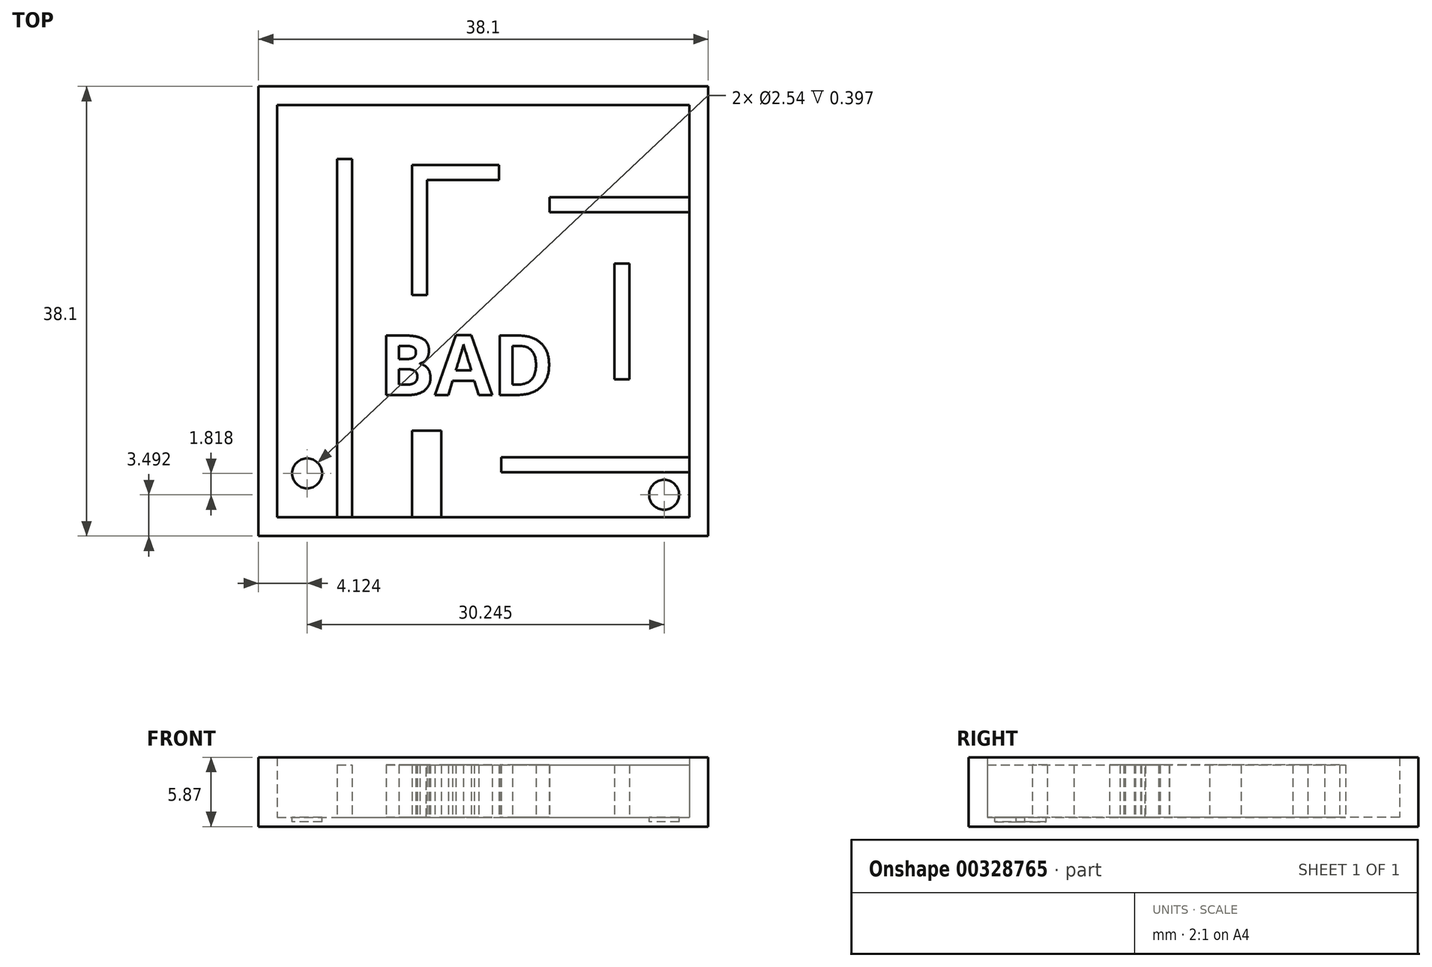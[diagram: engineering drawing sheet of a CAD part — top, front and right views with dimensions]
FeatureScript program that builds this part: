
annotation { "Feature Type Name" : "Feature", "Feature Type Description" : "" }
export const myFeature = defineFeature(function(context is Context, id is Id, definition is map)
    precondition{}
    {
        {
            var Q0;
            Q0=qCreatedBy(makeId("Top.planeOp"),FACE);
            var sketch = newSketch(context, id + "F0", { "sketchPlane" : qUnion([Q0])});
            skLineSegment(sketch, "E0.bottom", {"start": v(-16.01, 14.3) * mm, "end": v(22.09, 14.3) * mm});
            skLineSegment(sketch, "E0.top", {"start": v(-16.01, -23.8) * mm, "end": v(22.09, -23.8) * mm});
            skLineSegment(sketch, "E0.left", {"start": v(-16.01, 14.3) * mm, "end": v(-16.01, -23.8) * mm});
            skLineSegment(sketch, "E0.right", {"start": v(22.09, 14.3) * mm, "end": v(22.09, -23.8) * mm});
            skSolve(sketch);
        }
        {
            var Q0;
            Q0=makeQuery(id+"F0.imprint","IMPRINT",FACE,{"disambiguationData":[TD([[makeQuery(id+"F0.imprint","IMPRINT",EDGE,{"derivedFrom":sQuery(id+"F0.wireOp",EDGE,"E0.bottom")}),-1.0]])]});
            extrude(context, id + "F1", {"entities" : qUnion([Q0]), "depth" : 0.8 * mm});
        }
        {
            var Q0;
            Q0=makeQuery(id+"F1.opExtrude","CAP_FACE",FACE,{"disambiguationData":[OSD([sQuery(id+"F0.wireOp",EDGE,"E0.bottom"),sQuery(id+"F0.wireOp",EDGE,"E0.top"),sQuery(id+"F0.wireOp",EDGE,"E0.left"),sQuery(id+"F0.wireOp",EDGE,"E0.right")])],"isStart":false});
            var sketch = newSketch(context, id + "F2", { "sketchPlane" : qUnion([Q0])});
            skLineSegment(sketch, "E1.0", {"start": v(-14.43, 12.71) * mm, "end": v(20.5, 12.71) * mm});
            skLineSegment(sketch, "E1.1", {"start": v(-14.43, 12.71) * mm, "end": v(-14.43, -22.21) * mm});
            skLineSegment(sketch, "E1.2", {"start": v(-14.43, -22.21) * mm, "end": v(20.5, -22.21) * mm});
            skLineSegment(sketch, "E1.3", {"start": v(20.5, 12.71) * mm, "end": v(20.5, -22.21) * mm});
            skSolve(sketch);
        }
        {
            var Q0;
            Q0=makeQuery(id+"F2.imprint","IMPRINT",FACE,{"disambiguationData":[TD([[makeQuery(id+"F2.imprint","IMPRINT",EDGE,{"derivedFrom":sQuery(id+"F2.wireOp",EDGE,"E1.0")}),1.0]])]});
            extrude(context, id + "F3", {"entities" : qUnion([Q0]), "operationType" : NewBodyOperationType.ADD, "depth" : 5.08 * mm});
        }
        {
            var Q0;
            Q0=makeQuery(id+"F1.opExtrude","CAP_FACE",FACE,{"disambiguationData":[OSD([sQuery(id+"F0.wireOp",EDGE,"E0.bottom"),sQuery(id+"F0.wireOp",EDGE,"E0.top"),sQuery(id+"F0.wireOp",EDGE,"E0.left"),sQuery(id+"F0.wireOp",EDGE,"E0.right")])],"isStart":false});
            var sketch = newSketch(context, id + "F4", { "sketchPlane" : qUnion([Q0])});
            skLineSegment(sketch, "E2.bottom", {"start": v(4.57, -18.4) * mm, "end": v(20.5, -18.4) * mm});
            skLineSegment(sketch, "E2.top", {"start": v(4.57, -17.13) * mm, "end": v(20.5, -17.13) * mm});
            skLineSegment(sketch, "E2.right", {"start": v(20.5, -17.13) * mm, "end": v(20.5, -18.4) * mm});
            skLineSegment(sketch, "E3", {"start": v(4.57, -17.13) * mm, "end": v(4.57, -18.4) * mm});
            skLineSegment(sketch, "E4", {"start": v(-14.43, -22.21) * mm, "end": v(-14.43, -22.21) * mm});
            skCircle(sketch, "E5", {"center": v(-11.89, -18.49) * mm, "radius": 1.27 * mm});
            skLineSegment(sketch, "E6", {"start": v(20.5, -17.13) * mm, "end": v(20.5, -22.21) * mm});
            skLineSegment(sketch, "E7", {"start": v(20.5, -18.4) * mm, "end": v(20.5, -22.21) * mm});
            skPoint(sketch, "E8.centerSnap0", {"position": v(20.5, -20.3) * mm});
            skCircle(sketch, "E9", {"center": v(18.36, -20.3) * mm, "radius": 1.27 * mm});
            skText(sketch, "E10", { "text": "BAD", "fontName": "OpenSans-Bold.ttf"});
            skLineSegment(sketch, "E11.bottom", {"start": v(-9.35, -22.21) * mm, "end": v(-8.08, -22.21) * mm});
            skLineSegment(sketch, "E11.top", {"start": v(-9.35, 8.13) * mm, "end": v(-8.08, 8.13) * mm});
            skLineSegment(sketch, "E11.left", {"start": v(-9.35, -22.21) * mm, "end": v(-9.35, 8.13) * mm});
            skLineSegment(sketch, "E11.right", {"start": v(-8.08, -22.21) * mm, "end": v(-8.08, 8.13) * mm});
            skLineSegment(sketch, "E12.bottom", {"start": v(8.66, 4.92) * mm, "end": v(20.5, 4.92) * mm});
            skLineSegment(sketch, "E12.top", {"start": v(8.66, 3.65) * mm, "end": v(20.5, 3.65) * mm});
            skLineSegment(sketch, "E12.left", {"start": v(8.66, 4.92) * mm, "end": v(8.66, 3.65) * mm});
            skLineSegment(sketch, "E12.right", {"start": v(20.5, 4.92) * mm, "end": v(20.5, 3.65) * mm});
            skLineSegment(sketch, "E13.bottom", {"start": v(-3, -22.21) * mm, "end": v(-0.51, -22.21) * mm});
            skLineSegment(sketch, "E13.top", {"start": v(-3, -14.88) * mm, "end": v(-0.51, -14.88) * mm});
            skLineSegment(sketch, "E13.left", {"start": v(-3, -22.21) * mm, "end": v(-3, -14.88) * mm});
            skLineSegment(sketch, "E13.right", {"start": v(-0.51, -22.21) * mm, "end": v(-0.51, -14.88) * mm});
            skLineSegment(sketch, "E14.bottom", {"start": v(14.15, -0.73) * mm, "end": v(15.42, -0.73) * mm});
            skLineSegment(sketch, "E14.top", {"start": v(14.15, -10.53) * mm, "end": v(15.42, -10.53) * mm});
            skLineSegment(sketch, "E14.left", {"start": v(14.15, -0.73) * mm, "end": v(14.15, -10.53) * mm});
            skLineSegment(sketch, "E14.right", {"start": v(15.42, -0.73) * mm, "end": v(15.42, -10.53) * mm});
            skLineSegment(sketch, "E15.bottom", {"start": v(-3, 7.63) * mm, "end": v(4.39, 7.63) * mm});
            skLineSegment(sketch, "E15.top", {"start": v(-1.73, 6.36) * mm, "end": v(4.39, 6.36) * mm});
            skLineSegment(sketch, "E15.left", {"start": v(-3, 7.63) * mm, "end": v(-3, 6.36) * mm});
            skLineSegment(sketch, "E15.right", {"start": v(4.39, 7.63) * mm, "end": v(4.39, 6.36) * mm});
            skLineSegment(sketch, "E16.top", {"start": v(-3, -3.38) * mm, "end": v(-1.73, -3.38) * mm});
            skLineSegment(sketch, "E16.left", {"start": v(-3, 6.36) * mm, "end": v(-3, -3.38) * mm});
            skLineSegment(sketch, "E16.right", {"start": v(-1.73, 6.36) * mm, "end": v(-1.73, -3.38) * mm});
            const initialGuessF4  = {"E10": [-0.00581, -0.01185, 1, 0, 0.00508]};
            skSetInitialGuess(sketch, initialGuessF4);
            skSolve(sketch);
        }
        {
            var Q0;
            Q0=makeQuery(id+"F4.imprint","IMPRINT",FACE,{"disambiguationData":[TD([[makeQuery(id+"F4.imprint","IMPRINT",EDGE,{"derivedFrom":sQuery(id+"F4.wireOp",EDGE,"E5")}),1.0]])]});
            extrude(context, id + "F5", {"entities" : qUnion([Q0]), "operationType" : NewBodyOperationType.REMOVE, "oppositeDirection" : true, "depth" : 0.4 * mm});
        }
        {
            var Q0;
            Q0=makeQuery(id+"F4.imprint","IMPRINT",FACE,{"disambiguationData":[TD([[makeQuery(id+"F4.imprint","IMPRINT",EDGE,{"derivedFrom":sQuery(id+"F4.wireOp",EDGE,"E9")}),1.0]])]});
            extrude(context, id + "F6", {"entities" : qUnion([Q0]), "operationType" : NewBodyOperationType.REMOVE, "oppositeDirection" : true, "depth" : 0.4 * mm});
        }
        {
            var Q0;
            Q0=makeQuery(id+"F4.imprint","IMPRINT",FACE,{"disambiguationData":[TD([[makeQuery(id+"F4.imprint","IMPRINT",EDGE,{"derivedFrom":sQuery(id+"F4.wireOp",EDGE,"E11.bottom")}),1.0]])]});
            var Q1;
            Q1=makeQuery(id+"F4.imprint","IMPRINT",FACE,{"disambiguationData":[TD([[makeQuery(id+"F4.imprint","IMPRINT",EDGE,{"derivedFrom":sQuery(id+"F4.wireOp",EDGE,"E13.bottom")}),1.0]])]});
            var Q2;
            Q2=makeQuery(id+"F4.imprint","IMPRINT",FACE,{"disambiguationData":[TD([[makeQuery(id+"F4.imprint","IMPRINT",EDGE,{"derivedFrom":sQuery(id+"F4.wireOp",EDGE,"E2.bottom")}),1.0]])]});
            var Q3;
            Q3=makeQuery(id+"F4.imprint","IMPRINT",FACE,{"disambiguationData":[TD([[makeQuery(id+"F4.imprint","IMPRINT",EDGE,{"derivedFrom":sQuery(id+"F4.wireOp",EDGE,"E10.sketch_text.stroke-37")}),-1.0]])]});
            var Q4;
            Q4=makeQuery(id+"F4.imprint","IMPRINT",FACE,{"disambiguationData":[TD([[makeQuery(id+"F4.imprint","IMPRINT",EDGE,{"derivedFrom":sQuery(id+"F4.wireOp",EDGE,"E10.sketch_text.stroke-25")}),-1.0]])]});
            var Q5;
            Q5=makeQuery(id+"F4.imprint","IMPRINT",FACE,{"disambiguationData":[TD([[makeQuery(id+"F4.imprint","IMPRINT",EDGE,{"derivedFrom":sQuery(id+"F4.wireOp",EDGE,"E10.sketch_text.stroke-0")}),-1.0]])]});
            var Q6;
            Q6=makeQuery(id+"F4.imprint","IMPRINT",FACE,{"disambiguationData":[TD([[makeQuery(id+"F4.imprint","IMPRINT",EDGE,{"derivedFrom":sQuery(id+"F4.wireOp",EDGE,"E14.bottom")}),-1.0]])]});
            var Q7;
            Q7=makeQuery(id+"F4.imprint","IMPRINT",FACE,{"disambiguationData":[TD([[makeQuery(id+"F4.imprint","IMPRINT",EDGE,{"derivedFrom":sQuery(id+"F4.wireOp",EDGE,"E12.bottom")}),-1.0]])]});
            var Q8;
            Q8=makeQuery(id+"F4.imprint","IMPRINT",FACE,{"disambiguationData":[TD([[makeQuery(id+"F4.imprint","IMPRINT",EDGE,{"derivedFrom":sQuery(id+"F4.wireOp",EDGE,"E15.bottom")}),-1.0]])]});
            extrude(context, id + "F7", {"entities" : qUnion([Q0, Q1, Q2, Q3, Q4, Q5, Q6, Q7, Q8]), "operationType" : NewBodyOperationType.ADD, "depth" : 4.44 * mm});
        }
    });
